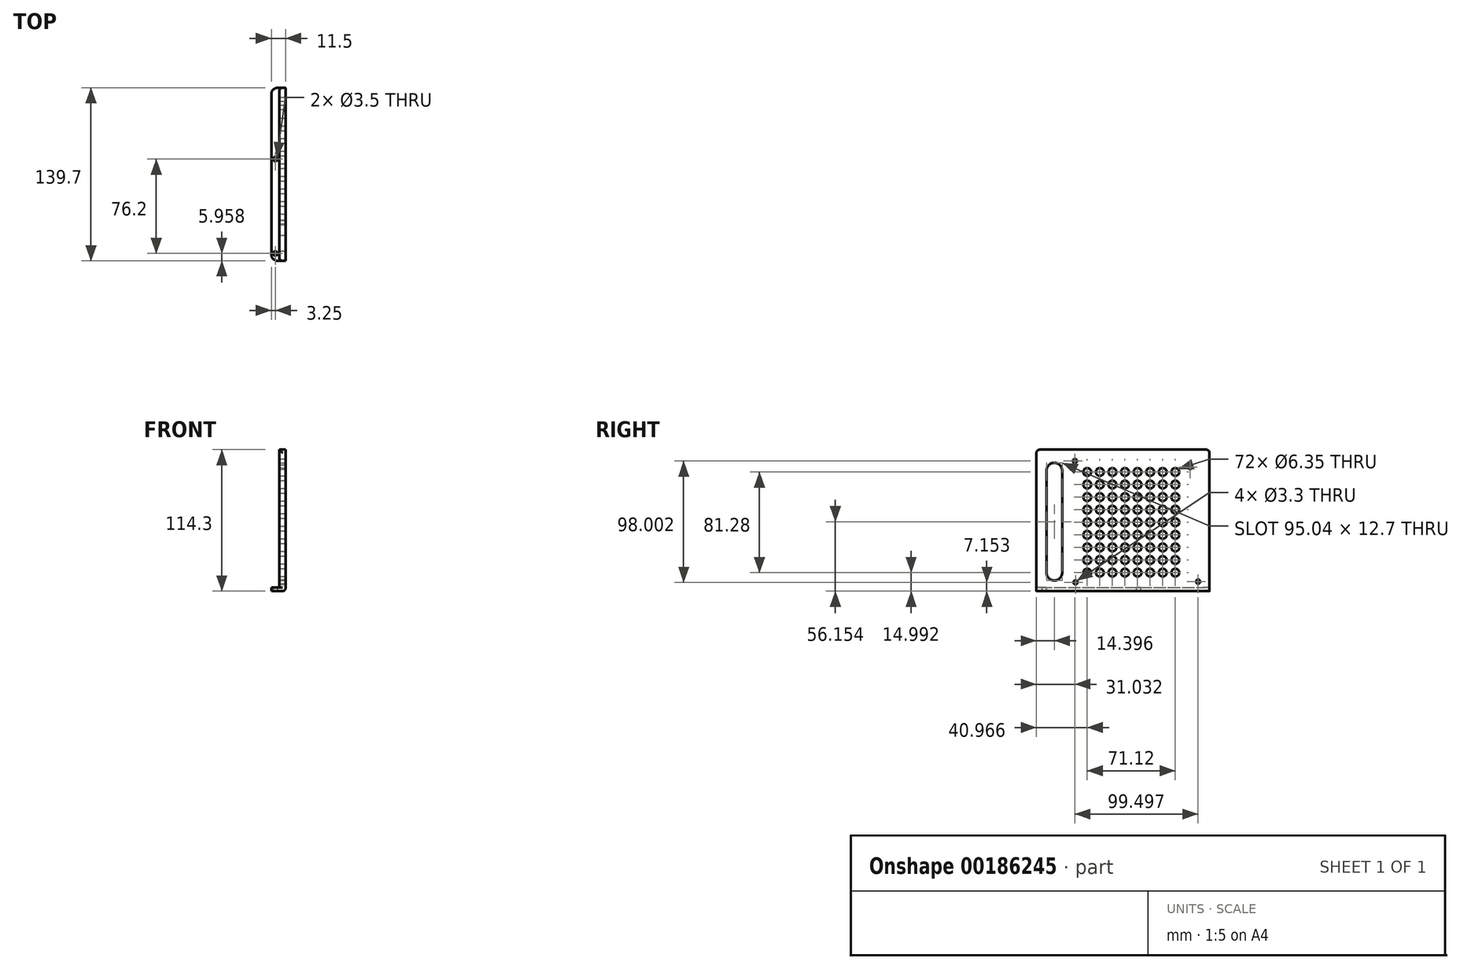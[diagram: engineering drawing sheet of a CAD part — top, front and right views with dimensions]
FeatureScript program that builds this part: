
annotation { "Feature Type Name" : "Feature", "Feature Type Description" : "" }
export const myFeature = defineFeature(function(context is Context, id is Id, definition is map)
    precondition{}
    {
        {
            var Q0;
            Q0=qCreatedBy(makeId("Top.planeOp"),FACE);
            var sketch = newSketch(context, id + "F0", { "sketchPlane" : qUnion([Q0])});
            skLineSegment(sketch, "E0.bottom", {"start": v(0, 0) * mm, "end": v(6.5, 0) * mm});
            skLineSegment(sketch, "E0.top", {"start": v(0, 139.7) * mm, "end": v(6.5, 139.7) * mm});
            skLineSegment(sketch, "E0.left", {"start": v(0, 0) * mm, "end": v(0, 139.7) * mm});
            skLineSegment(sketch, "E0.right", {"start": v(6.5, 0) * mm, "end": v(6.5, 139.7) * mm});
            skCircle(sketch, "E1", {"center": v(3.25, 82.16) * mm, "radius": 1.75 * mm});
            skCircle(sketch, "E2", {"center": v(3.25, 5.96) * mm, "radius": 1.75 * mm});
            skLineSegment(sketch, "E3.bottom", {"start": v(6.5, 139.7) * mm, "end": v(11.5, 139.7) * mm});
            skLineSegment(sketch, "E3.top", {"start": v(6.5, 0) * mm, "end": v(11.5, 0) * mm});
            skLineSegment(sketch, "E3.left", {"start": v(6.5, 139.7) * mm, "end": v(6.5, 0) * mm});
            skLineSegment(sketch, "E3.right", {"start": v(11.5, 139.7) * mm, "end": v(11.5, 0) * mm});
            skPoint(sketch, "E4", {"position": v(3.25, 0) * mm});
            skSolve(sketch);
        }
        {
            var Q0;
            Q0=makeQuery(id+"F0.imprint","IMPRINT",FACE,{"disambiguationData":[TD([[makeQuery(id+"F0.imprint","IMPRINT",EDGE,{"derivedFrom":sQuery(id+"F0.wireOp",EDGE,"E0.bottom")}),1.0]])]});
            extrude(context, id + "F1", {"entities" : qUnion([Q0]), "depth" : 3 * mm});
        }
        {
            var Q0;
            Q0=makeQuery(id+"F0.imprint","IMPRINT",FACE,{"disambiguationData":[TD([[makeQuery(id+"F0.imprint","IMPRINT",EDGE,{"derivedFrom":sQuery(id+"F0.wireOp",EDGE,"E3.bottom")}),-1.0]])]});
            extrude(context, id + "F2", {"entities" : qUnion([Q0]), "operationType" : NewBodyOperationType.ADD, "depth" : 114.3 * mm});
        }
        {
            var Q0;
            Q0=makeQuery(id+"F2.opExtrude","SWEPT_FACE",FACE,{"disambiguationData":[OSD([sQuery(id+"F0.wireOp",EDGE,"E3.right")])]});
            var sketch = newSketch(context, id + "F3", { "sketchPlane" : qUnion([Q0])});
            skCircle(sketch, "E5", {"center": v(31.03, 105.15) * mm, "radius": 1.65 * mm});
            skCircle(sketch, "E6", {"center": v(31.53, 7.15) * mm, "radius": 1.65 * mm});
            skCircle(sketch, "E7", {"center": v(124.03, 100.26) * mm, "radius": 1.65 * mm});
            skCircle(sketch, "E8", {"center": v(130.53, 7.76) * mm, "radius": 1.65 * mm});
            skLineSegment(sketch, "E9.bottom", {"start": v(3.03, 108.75) * mm, "end": v(133.03, 108.75) * mm, "construction": true});
            skLineSegment(sketch, "E9.top", {"start": v(3.03, 3.55) * mm, "end": v(133.03, 3.55) * mm, "construction": true});
            skLineSegment(sketch, "E9.left", {"start": v(3.03, 108.75) * mm, "end": v(3.03, 3.55) * mm, "construction": true});
            skLineSegment(sketch, "E9.right", {"start": v(133.03, 108.75) * mm, "end": v(133.03, 3.55) * mm, "construction": true});
            skCircle(sketch, "E10", {"center": v(40.97, 96.27) * mm, "radius": 3.18 * mm});
            skCircle(sketch, "E11.0.1.0", {"center": v(40.97, 86.11) * mm, "radius": 3.18 * mm});
            skCircle(sketch, "E11.0.2.0", {"center": v(40.97, 75.95) * mm, "radius": 3.18 * mm});
            skCircle(sketch, "E11.0.3.0", {"center": v(40.97, 65.8) * mm, "radius": 3.18 * mm});
            skCircle(sketch, "E11.0.4.0", {"center": v(40.97, 55.63) * mm, "radius": 3.18 * mm});
            skCircle(sketch, "E11.0.5.0", {"center": v(40.97, 45.47) * mm, "radius": 3.18 * mm});
            skCircle(sketch, "E11.0.6.0", {"center": v(40.97, 35.31) * mm, "radius": 3.18 * mm});
            skCircle(sketch, "E11.0.7.0", {"center": v(40.97, 25.15) * mm, "radius": 3.18 * mm});
            skCircle(sketch, "E11.0.8.0", {"center": v(40.97, 15) * mm, "radius": 3.18 * mm});
            skCircle(sketch, "E11.1.0.0", {"center": v(51.13, 96.27) * mm, "radius": 3.18 * mm});
            skCircle(sketch, "E11.1.1.0", {"center": v(51.13, 86.11) * mm, "radius": 3.18 * mm});
            skCircle(sketch, "E11.1.2.0", {"center": v(51.13, 75.95) * mm, "radius": 3.18 * mm});
            skCircle(sketch, "E11.1.3.0", {"center": v(51.13, 65.8) * mm, "radius": 3.18 * mm});
            skCircle(sketch, "E11.1.4.0", {"center": v(51.13, 55.63) * mm, "radius": 3.18 * mm});
            skCircle(sketch, "E11.1.5.0", {"center": v(51.13, 45.47) * mm, "radius": 3.18 * mm});
            skCircle(sketch, "E11.1.6.0", {"center": v(51.13, 35.31) * mm, "radius": 3.18 * mm});
            skCircle(sketch, "E11.1.7.0", {"center": v(51.13, 25.15) * mm, "radius": 3.18 * mm});
            skCircle(sketch, "E11.1.8.0", {"center": v(51.13, 15) * mm, "radius": 3.18 * mm});
            skCircle(sketch, "E11.2.0.0", {"center": v(61.29, 96.27) * mm, "radius": 3.18 * mm});
            skCircle(sketch, "E11.2.1.0", {"center": v(61.29, 86.11) * mm, "radius": 3.18 * mm});
            skCircle(sketch, "E11.2.2.0", {"center": v(61.29, 75.95) * mm, "radius": 3.18 * mm});
            skCircle(sketch, "E11.2.3.0", {"center": v(61.29, 65.8) * mm, "radius": 3.18 * mm});
            skCircle(sketch, "E11.2.4.0", {"center": v(61.29, 55.63) * mm, "radius": 3.18 * mm});
            skCircle(sketch, "E11.2.5.0", {"center": v(61.29, 45.47) * mm, "radius": 3.18 * mm});
            skCircle(sketch, "E11.2.6.0", {"center": v(61.29, 35.31) * mm, "radius": 3.18 * mm});
            skCircle(sketch, "E11.2.7.0", {"center": v(61.29, 25.15) * mm, "radius": 3.18 * mm});
            skCircle(sketch, "E11.2.8.0", {"center": v(61.29, 15) * mm, "radius": 3.18 * mm});
            skCircle(sketch, "E11.3.0.0", {"center": v(71.45, 96.27) * mm, "radius": 3.18 * mm});
            skCircle(sketch, "E11.3.1.0", {"center": v(71.45, 86.11) * mm, "radius": 3.18 * mm});
            skCircle(sketch, "E11.3.2.0", {"center": v(71.45, 75.95) * mm, "radius": 3.18 * mm});
            skCircle(sketch, "E11.3.3.0", {"center": v(71.45, 65.8) * mm, "radius": 3.18 * mm});
            skCircle(sketch, "E11.3.4.0", {"center": v(71.45, 55.63) * mm, "radius": 3.18 * mm});
            skCircle(sketch, "E11.3.5.0", {"center": v(71.45, 45.47) * mm, "radius": 3.18 * mm});
            skCircle(sketch, "E11.3.6.0", {"center": v(71.45, 35.31) * mm, "radius": 3.18 * mm});
            skCircle(sketch, "E11.3.7.0", {"center": v(71.45, 25.15) * mm, "radius": 3.18 * mm});
            skCircle(sketch, "E11.3.8.0", {"center": v(71.45, 15) * mm, "radius": 3.18 * mm});
            skCircle(sketch, "E11.4.0.0", {"center": v(81.6, 96.27) * mm, "radius": 3.18 * mm});
            skCircle(sketch, "E11.4.1.0", {"center": v(81.6, 86.11) * mm, "radius": 3.18 * mm});
            skCircle(sketch, "E11.4.2.0", {"center": v(81.6, 75.95) * mm, "radius": 3.18 * mm});
            skCircle(sketch, "E11.4.3.0", {"center": v(81.6, 65.8) * mm, "radius": 3.18 * mm});
            skCircle(sketch, "E11.4.4.0", {"center": v(81.6, 55.63) * mm, "radius": 3.18 * mm});
            skCircle(sketch, "E11.4.5.0", {"center": v(81.6, 45.47) * mm, "radius": 3.18 * mm});
            skCircle(sketch, "E11.4.6.0", {"center": v(81.6, 35.31) * mm, "radius": 3.18 * mm});
            skCircle(sketch, "E11.4.7.0", {"center": v(81.6, 25.15) * mm, "radius": 3.18 * mm});
            skCircle(sketch, "E11.4.8.0", {"center": v(81.6, 15) * mm, "radius": 3.18 * mm});
            skCircle(sketch, "E11.5.0.0", {"center": v(91.77, 96.27) * mm, "radius": 3.18 * mm});
            skCircle(sketch, "E11.5.1.0", {"center": v(91.77, 86.11) * mm, "radius": 3.18 * mm});
            skCircle(sketch, "E11.5.2.0", {"center": v(91.77, 75.95) * mm, "radius": 3.18 * mm});
            skCircle(sketch, "E11.5.3.0", {"center": v(91.77, 65.8) * mm, "radius": 3.18 * mm});
            skCircle(sketch, "E11.5.4.0", {"center": v(91.77, 55.63) * mm, "radius": 3.18 * mm});
            skCircle(sketch, "E11.5.5.0", {"center": v(91.77, 45.47) * mm, "radius": 3.18 * mm});
            skCircle(sketch, "E11.5.6.0", {"center": v(91.77, 35.31) * mm, "radius": 3.18 * mm});
            skCircle(sketch, "E11.5.7.0", {"center": v(91.77, 25.15) * mm, "radius": 3.18 * mm});
            skCircle(sketch, "E11.5.8.0", {"center": v(91.77, 15) * mm, "radius": 3.18 * mm});
            skCircle(sketch, "E11.6.0.0", {"center": v(101.93, 96.27) * mm, "radius": 3.18 * mm});
            skCircle(sketch, "E11.6.1.0", {"center": v(101.93, 86.11) * mm, "radius": 3.18 * mm});
            skCircle(sketch, "E11.6.2.0", {"center": v(101.93, 75.95) * mm, "radius": 3.18 * mm});
            skCircle(sketch, "E11.6.3.0", {"center": v(101.93, 65.8) * mm, "radius": 3.18 * mm});
            skCircle(sketch, "E11.6.4.0", {"center": v(101.93, 55.63) * mm, "radius": 3.18 * mm});
            skCircle(sketch, "E11.6.5.0", {"center": v(101.93, 45.47) * mm, "radius": 3.18 * mm});
            skCircle(sketch, "E11.6.6.0", {"center": v(101.93, 35.31) * mm, "radius": 3.18 * mm});
            skCircle(sketch, "E11.6.7.0", {"center": v(101.93, 25.15) * mm, "radius": 3.18 * mm});
            skCircle(sketch, "E11.6.8.0", {"center": v(101.93, 15) * mm, "radius": 3.18 * mm});
            skCircle(sketch, "E11.7.0.0", {"center": v(112.09, 96.27) * mm, "radius": 3.18 * mm});
            skCircle(sketch, "E11.7.1.0", {"center": v(112.09, 86.11) * mm, "radius": 3.18 * mm});
            skCircle(sketch, "E11.7.2.0", {"center": v(112.09, 75.95) * mm, "radius": 3.18 * mm});
            skCircle(sketch, "E11.7.3.0", {"center": v(112.09, 65.8) * mm, "radius": 3.18 * mm});
            skCircle(sketch, "E11.7.4.0", {"center": v(112.09, 55.63) * mm, "radius": 3.18 * mm});
            skCircle(sketch, "E11.7.5.0", {"center": v(112.09, 45.47) * mm, "radius": 3.18 * mm});
            skCircle(sketch, "E11.7.6.0", {"center": v(112.09, 35.31) * mm, "radius": 3.18 * mm});
            skCircle(sketch, "E11.7.7.0", {"center": v(112.09, 25.15) * mm, "radius": 3.18 * mm});
            skCircle(sketch, "E11.7.8.0", {"center": v(112.09, 15) * mm, "radius": 3.18 * mm});
            skLineSegment(sketch, "E11.direction1", {"start": v(40.97, 96.27) * mm, "end": v(51.13, 96.27) * mm, "construction": true});
            skLineSegment(sketch, "E11.direction2", {"start": v(40.97, 96.27) * mm, "end": v(40.97, 86.11) * mm, "construction": true});
            skLineSegment(sketch, "E12", {"start": v(14.4, 97.32) * mm, "end": v(14.4, 14.98) * mm});
            skArc(sketch, "E13.0.startCap", {"start": v(8.05, 97.32) * mm, "mid": v(14.4, 103.67) * mm, "end": v(20.75, 97.32) * mm});
            skArc(sketch, "E13.0.endCap", {"start": v(20.75, 14.98) * mm, "mid": v(14.4, 8.63) * mm, "end": v(8.05, 14.98) * mm});
            skLineSegment(sketch, "E13.0.left", {"start": v(20.75, 97.32) * mm, "end": v(20.75, 14.98) * mm});
            skLineSegment(sketch, "E13.0.right", {"start": v(8.05, 97.32) * mm, "end": v(8.05, 14.98) * mm});
            skSolve(sketch);
        }
        {
            var Q0;
            Q0 = qSketchRegion(id + "F3", true);
            extrude(context, id + "F4", {"entities" : qUnion([Q0]), "operationType" : NewBodyOperationType.REMOVE, "oppositeDirection" : true, "depth" : 25.4 * mm});
        }
        {
            var Q0;
            Q0=makeQuery(id+"F2.opExtrude","CAP_EDGE",EDGE,{"disambiguationData":[OSD([sQuery(id+"F0.wireOp",EDGE,"E3.right")])],"isStart":true});
            var Q1;
            Q1=makeQuery(id+"F2.opExtrude","CAP_EDGE",EDGE,{"disambiguationData":[OSD([sQuery(id+"F0.wireOp",EDGE,"E3.left")])],"isStart":false});
            var Q2;
            Q2=makeQuery(id+"F2.opExtrude","SWEPT_EDGE",EDGE,{"disambiguationData":[OSD([sQuery(id+"F0.wireOp",EDGE,"E0.bottom"),sQuery(id+"F0.wireOp",EDGE,"E3.top"),sQuery(id+"F0.wireOp",EDGE,"E3.left")])]});
            var Q3;
            Q3=makeQuery(id+"F2.opExtrude","SWEPT_EDGE",EDGE,{"disambiguationData":[OSD([sQuery(id+"F0.wireOp",EDGE,"E0.top"),sQuery(id+"F0.wireOp",EDGE,"E3.bottom"),sQuery(id+"F0.wireOp",EDGE,"E3.left")])]});
            var Q4;
            Q4=makeQuery(id+"F2.opExtrude","CAP_EDGE",EDGE,{"disambiguationData":[OSD([sQuery(id+"F0.wireOp",EDGE,"E3.bottom")])],"isStart":false});
            var Q5;
            Q5=makeQuery(id+"F2.opExtrude","CAP_EDGE",EDGE,{"disambiguationData":[OSD([sQuery(id+"F0.wireOp",EDGE,"E3.top")])],"isStart":false});
            fillet(context, id + "F5", {"entities" : qUnion([Q0, Q1, Q2, Q3, Q4, Q5]), "radius" : 2.54 * mm, "tangentPropagation" : true, "allowEdgeOverflow" : false});
        }
        {
            var Q0;
            Q0=makeQuery(id+"F1.opExtrude","SWEPT_EDGE",EDGE,{"disambiguationData":[OSD([sQuery(id+"F0.wireOp",EDGE,"E0.bottom"),sQuery(id+"F0.wireOp",EDGE,"E0.left")])]});
            var Q1;
            Q1=makeQuery(id+"F1.opExtrude","SWEPT_EDGE",EDGE,{"disambiguationData":[OSD([sQuery(id+"F0.wireOp",EDGE,"E0.top"),sQuery(id+"F0.wireOp",EDGE,"E0.left")])]});
            fillet(context, id + "F6", {"entities" : qUnion([Q0, Q1]), "radius" : 5.08 * mm, "tangentPropagation" : true, "allowEdgeOverflow" : false});
        }
    });
